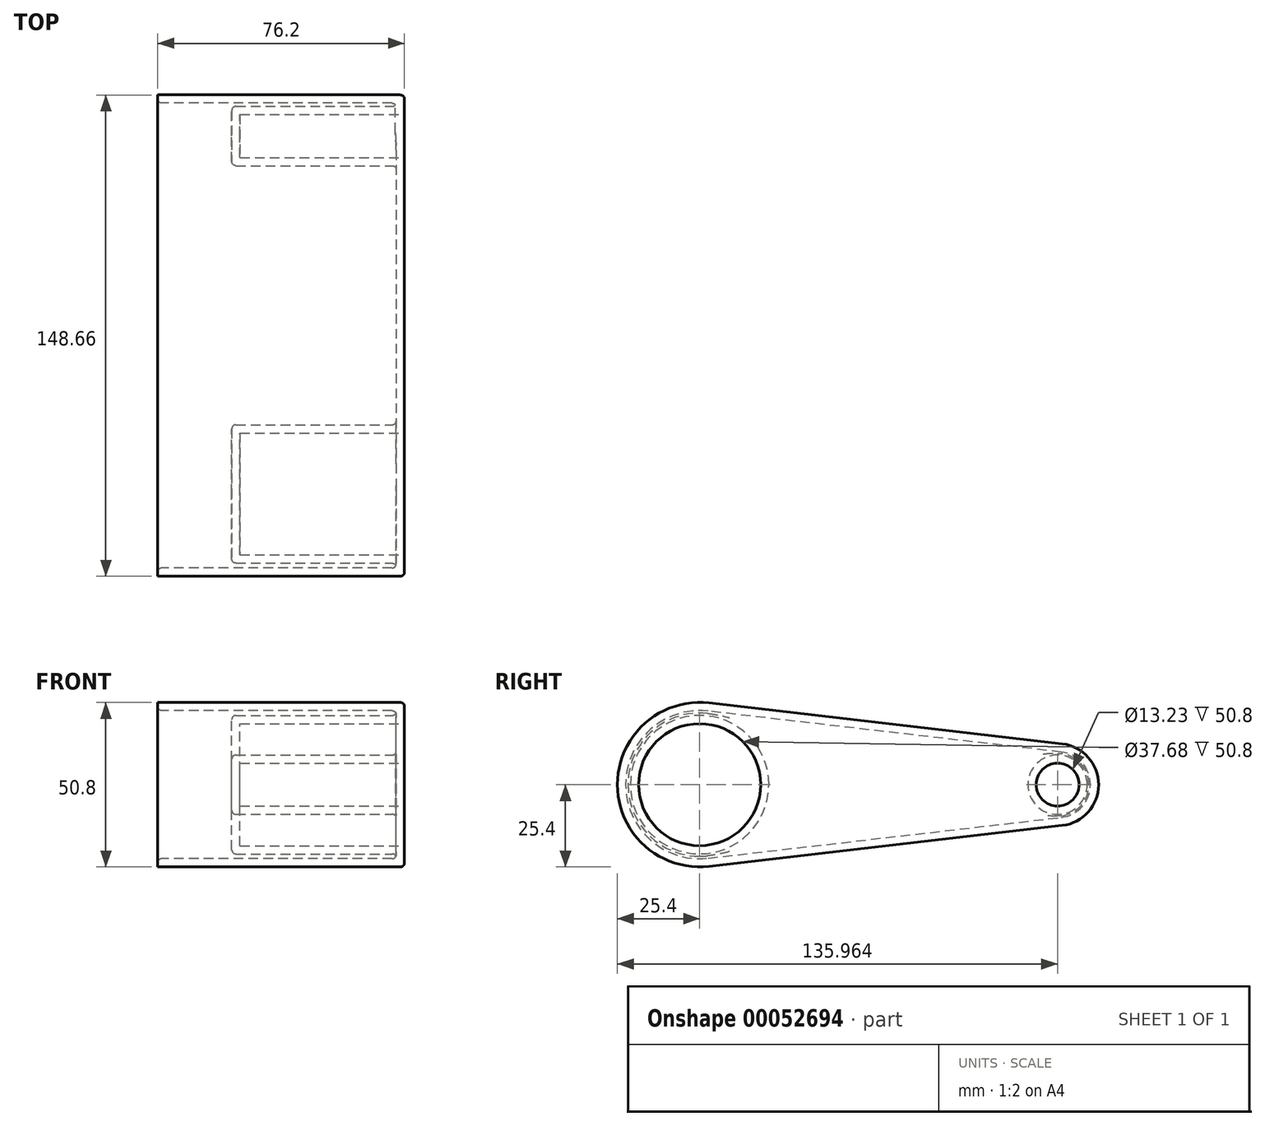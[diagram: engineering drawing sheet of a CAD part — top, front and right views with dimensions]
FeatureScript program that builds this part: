
annotation { "Feature Type Name" : "Feature", "Feature Type Description" : "" }
export const myFeature = defineFeature(function(context is Context, id is Id, definition is map)
    precondition{}
    {
        {
            var Q0;
            Q0=qCreatedBy(makeId("Right.planeOp"),FACE);
            var sketch = newSketch(context, id + "F0", { "sketchPlane" : qUnion([Q0])});
            skCircle(sketch, "E0", {"center": v(0, 0) * mm, "radius": 25.4 * mm});
            skCircle(sketch, "E1", {"center": v(110.56, 0) * mm, "radius": 12.7 * mm});
            skLineSegment(sketch, "E2", {"start": v(2.92, 25.23) * mm, "end": v(112.02, 12.62) * mm});
            skLineSegment(sketch, "E3", {"start": v(2.92, -25.23) * mm, "end": v(112.02, -12.62) * mm});
            skSolve(sketch);
        }
        {
            var Q0;
            Q0 = qSketchRegion(id + "F0", true);
            extrude(context, id + "F1", {"entities" : qUnion([Q0]), "depth" : 76.2 * mm});
        }
        {
            var Q0;
            Q0=makeQuery(id+"F1.opExtrude","CAP_FACE",FACE,{"disambiguationData":[OSD([sQuery(id+"F0.wireOp",EDGE,"E0"),sQuery(id+"F0.wireOp",EDGE,"E1"),sQuery(id+"F0.wireOp",EDGE,"E2"),sQuery(id+"F0.wireOp",EDGE,"E3")])],"isStart":false});
            var sketch = newSketch(context, id + "F2", { "sketchPlane" : qUnion([Q0])});
            skCircle(sketch, "E4", {"center": v(0, 0) * mm, "radius": 18.84 * mm});
            skCircle(sketch, "E5", {"center": v(110.56, 0) * mm, "radius": 6.61 * mm});
            skSolve(sketch);
        }
        {
            var Q0;
            Q0 = qSketchRegion(id + "F2", true);
            extrude(context, id + "F3", {"entities" : qUnion([Q0]), "operationType" : NewBodyOperationType.REMOVE, "oppositeDirection" : true, "depth" : 50.8 * mm});
        }
        {
            var Q0;
            Q0=makeQuery(id+"F1.opExtrude","CAP_EDGE",EDGE,{"disambiguationData":[OSD([sQuery(id+"F0.wireOp",EDGE,"E0")])],"isStart":false});
            var Q1;
            Q1=makeQuery(id+"F3.boolean.opBoolean","COPY",EDGE,{"derivedFrom":makeQuery(id+"F3.opExtrude","CAP_EDGE",EDGE,{"disambiguationData":[OSD([sQuery(id+"F2.wireOp",EDGE,"E4")])],"isStart":true})});
            var Q2;
            Q2=makeQuery(id+"F3.boolean.opBoolean","COPY",EDGE,{"derivedFrom":makeQuery(id+"F3.opExtrude","CAP_EDGE",EDGE,{"disambiguationData":[OSD([sQuery(id+"F2.wireOp",EDGE,"E5")])],"isStart":true})});
            fillet(context, id + "F4", {"entities" : qUnion([Q0, Q1, Q2]), "radius" : 1.27 * mm, "tangentPropagation" : true, "allowEdgeOverflow" : false});
        }
        {
            var Q0;
            Q0=makeQuery(id+"F1.opExtrude","CAP_FACE",FACE,{"disambiguationData":[OSD([sQuery(id+"F0.wireOp",EDGE,"E0"),sQuery(id+"F0.wireOp",EDGE,"E1"),sQuery(id+"F0.wireOp",EDGE,"E2"),sQuery(id+"F0.wireOp",EDGE,"E3")])],"isStart":true});
            shell(context, id + "F5", {"entities" : qUnion([Q0]), "thickness" : 2.54 * mm});
        }
        {
            var Q0;
            Q0=makeQuery(id+"F5.opShell","OFFSET_EDGE",EDGE,{"disambiguationData":[OSD([sQuery(id+"F0.wireOp",EDGE,"E2")])]});
            fillet(context, id + "F6", {"entities" : qUnion([Q0]), "radius" : 1.27 * mm, "tangentPropagation" : true, "allowEdgeOverflow" : false});
        }
        {
            var Q0;
            Q0=makeQuery(id+"F5.opShell","OFFSET_EDGE",EDGE,{"disambiguationData":[OSD([sQuery(id+"F2.wireOp",EDGE,"E5")])]});
            fillet(context, id + "F7", {"entities" : qUnion([Q0]), "radius" : 1.27 * mm, "tangentPropagation" : true, "allowEdgeOverflow" : false});
        }
        {
            var Q0;
            Q0=makeQuery(id+"F5.opShell","OFFSET_EDGE",EDGE,{"disambiguationData":[OSD([sQuery(id+"F2.wireOp",EDGE,"E4")])]});
            var Q1;
            Q1=makeQuery(id+"F5.opShell","OFFSET_FACE",FACE,{"disambiguationData":[OSD([sQuery(id+"F0.wireOp",EDGE,"E0"),sQuery(id+"F0.wireOp",EDGE,"E1"),sQuery(id+"F0.wireOp",EDGE,"E2"),sQuery(id+"F0.wireOp",EDGE,"E3")])]});
            fillet(context, id + "F8", {"entities" : qUnion([Q0, Q1]), "radius" : 1.27 * mm, "tangentPropagation" : true, "allowEdgeOverflow" : false});
        }
    });
